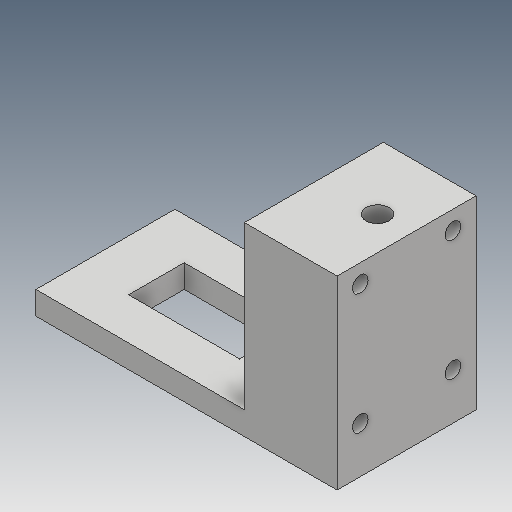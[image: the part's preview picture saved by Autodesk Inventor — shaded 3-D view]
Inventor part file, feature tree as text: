
AUTODESK INVENTOR PART (.ipt)
format: ipt  version: 2018 (Build 220112000, 112)  size: 118,784 bytes
history: native  units: mm
features: sketch x5, other x3
ambient origin geometry x8: Origin, YZ Plane, XZ Plane, XY Plane, X Axis, Y Axis, Z Axis, Center Point
bodies: Volumenkörper1 (feature_tree)
feature tree (8):
  other  "L-Halterung Servo.ipt"
  other  "Volumenkörper1::L-Halterung Servo.ipt"
  other  "Bezeichnung1"
  sketch  "Skizze1"  dims[d0=10.0mm]
  sketch  "Skizze2"
  sketch  "Skizze3"
  sketch  "Skizze4"
  sketch  "Skizze5"
